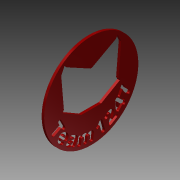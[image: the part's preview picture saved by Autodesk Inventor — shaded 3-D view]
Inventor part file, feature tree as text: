
AUTODESK INVENTOR PART (.ipt)
format: ipt  version: 2014 (Build 180170000, 170)  size: 1,403,392 bytes
history: native  units: in
note: dims shown in document units (in); Inventor stores cm internally (conversion verified against a paired STEP export)
features: sketch x23, extrude x16, plane x9, projected_geometry x8, loft x4, other x4, fillet x2, mirror x1, chamfer x1
ambient origin geometry x8: Origin, YZ Plane, XZ Plane, XY Plane, X Axis, Y Axis, Z Axis, Center Point
bodies: Solid1 (feature_tree)
feature tree (68):
  sketch  "Sketch1"  dims[d0=0.7559in d1=0.7559in]
  plane  "Work Plane1"
  loft  "Main Body"
  extrude  "Right Eye"  Depth=0.2in
  plane  "Work Plane4"
  loft  "Main Nose"
  plane  "Work Plane5"
  loft  "Back of Head"
  loft  "Main Ear - Right"
  extrude  "Inside of Ear - Right"  TaperAngle=0.0deg  [1 undecoded]
  plane  "Work Plane6"
  extrude  "Top and TopSide Rivets - Long"  Depth=1.0in
  extrude  "Top Most Rivet -  Cut Down"  Depth=1.0651in
  extrude  "Top Lower Rivet - Cut Down"  Depth=0.962in
  plane  "Work Plane7"
  extrude  "Side Rivets"  Depth=0.075in
  plane  "Work Plane8"
  other  "Work Axis1"
  plane  "Work Plane9"
  extrude  "Ear Shaping - Right"  Depth=0.06in
  mirror  "Eye, Ear and Rivet Mirro"
  extrude  "Fill Back (Make it a flat Print)"  Depth=0.05in
  plane  "Work Plane10"
  extrude  "Fill Back 2"  Depth=0.0625in
  plane  "Work Plane11"
  extrude  "Cut Back 1 (Adjust Angle)"  Depth=0.075in
  extrude  "Cut Back 2"  TaperAngle=0.0deg  [1 undecoded]
  extrude  "Round Back"  Depth=0.2in
  extrude  "Lip"  TaperAngle=0.0deg  [1 undecoded]
  other  "Team Text"
  extrude  "Remove Area for Ears"  Depth=0.01in
  extrude  "Remove Area for Nose"  Depth=0.0344in
  chamfer  "Chamfer Eyes"  Distance=0.05in
  fillet  "Fill Bridge of Nose"  Radius=0.05in
  fillet  "Fillet3"  Radius=0.05in
  extrude  "Extrusion19"  Depth=0.05in
  sketch  "Sketch2"  dims[d2=0.9963in d3=0.2in]
  sketch  "Sketch3"  dims[d4=0.5in d6=0.08in]
  sketch  "Sketch4"  dims[d7=0.55in d8=150.0deg]
  other  "Edges1"
  sketch  "Sketch5"  dims[d9=150.0deg d14=0.33in]
  projected_geometry  "Projected Loop1"
  other  "Edges2"
  sketch  "Sketch6"  dims[d15=0.66in d18=0.0in d19=90.0deg]
  sketch  "Sketch7"  dims[d20=0.0in d21=90.0deg d22=1.0in]
  sketch  "Sketch8"  dims[d26=1.0651in d28=1.0651in]
  sketch  "Sketch9"  dims[d29=0.0in d30=0.962in]
  sketch  "Sketch10"  dims[d31=0.962in d32=0.075in]
  sketch  "Sketch11"  dims[d33=0.15in d34=0.06in]
  sketch  "Sketch12"  dims[d35=0.1in d36=0.05in]
  sketch  "Sketch13"  dims[d37=0.45in d38=0.0in d39=0.0625in]
  projected_geometry  "Projected Loop2"
  projected_geometry  "Projected Loop3"
  sketch  "Sketch14"  dims[d40=0.01in d41=0.075in]
  projected_geometry  "Projected Loop4"
  sketch  "Sketch15"  dims[d42=0.01in d43=0.0in d44=90.0deg]
  sketch  "Sketch16"  dims[d45=0.0in d46=90.0deg d47=0.2in]
  sketch  "Sketch17"  dims[d48=0.07in d49=0.0in d50=90.0deg]
  sketch  "Sketch18"  dims[d51=0.0in d52=90.0deg d53=0.01in]
  sketch  "Sketch19"  dims[d54=0.01in d55=0.0344in]
  sketch  "Sketch20"  dims[d56=150.0deg]
  sketch  "Sketch23"  dims[d57=60.0deg]
  projected_geometry  "Projected Loop6"
  sketch  "Sketch24"  dims[d58=150.0deg]
  sketch  "Sketch26"  dims[d59=0.7in d60=0.05in d61=0.05in d62=0.05in d63=0.05in d64=0.05in d65=0.01in d66=0.0in d67=90.0deg d68=0.0in d69=90.0deg d70=0.1in d71=0.4in d72=0.15in d73=0.05in d74=0.0in d75=0.02in d77=0.15in d78=0.02in d79=0.1in d80=0.1in d81=0.1in d82=0.02in d83=0.15in d84=0.05in d85=0.0in d86=0.045in d87=0.0in d88=0.025in d89=0.0in d90=0.02in d91=0.02in d92=0.005in d93=0.0in d94=90.0deg d95=0.4466in d96=1.0in d97=0.0in d98=1.0in d99=0.0in d100=0.6528in d101=0.0in d102=0.0in d103=1.0in d104=0.0in d106=90.0deg d107=1.0in d108=0.0in d109=1.65in d110=0.1in d111=0.075in d112=0.0in d113=0.1in d114=0.075in d115=0.0in d116=0.05in d117=0.0in d123=0.1in d124=0.0in d125=0.05in d126=0.0in d130=0.02in d131=0.125in d132=45.0deg d133=0.02in d137=0.02in d138=0.0375in d139=0.0in]
  projected_geometry  "Projected Loop10"
  projected_geometry  "Projected Loop11"
  projected_geometry  "Projected Loop12"
note: 3 required parameter values undecoded (feature->parameter linkage not recoverable at this tier; creation-order binding heuristic only, values carry confidence <= 0.55)
